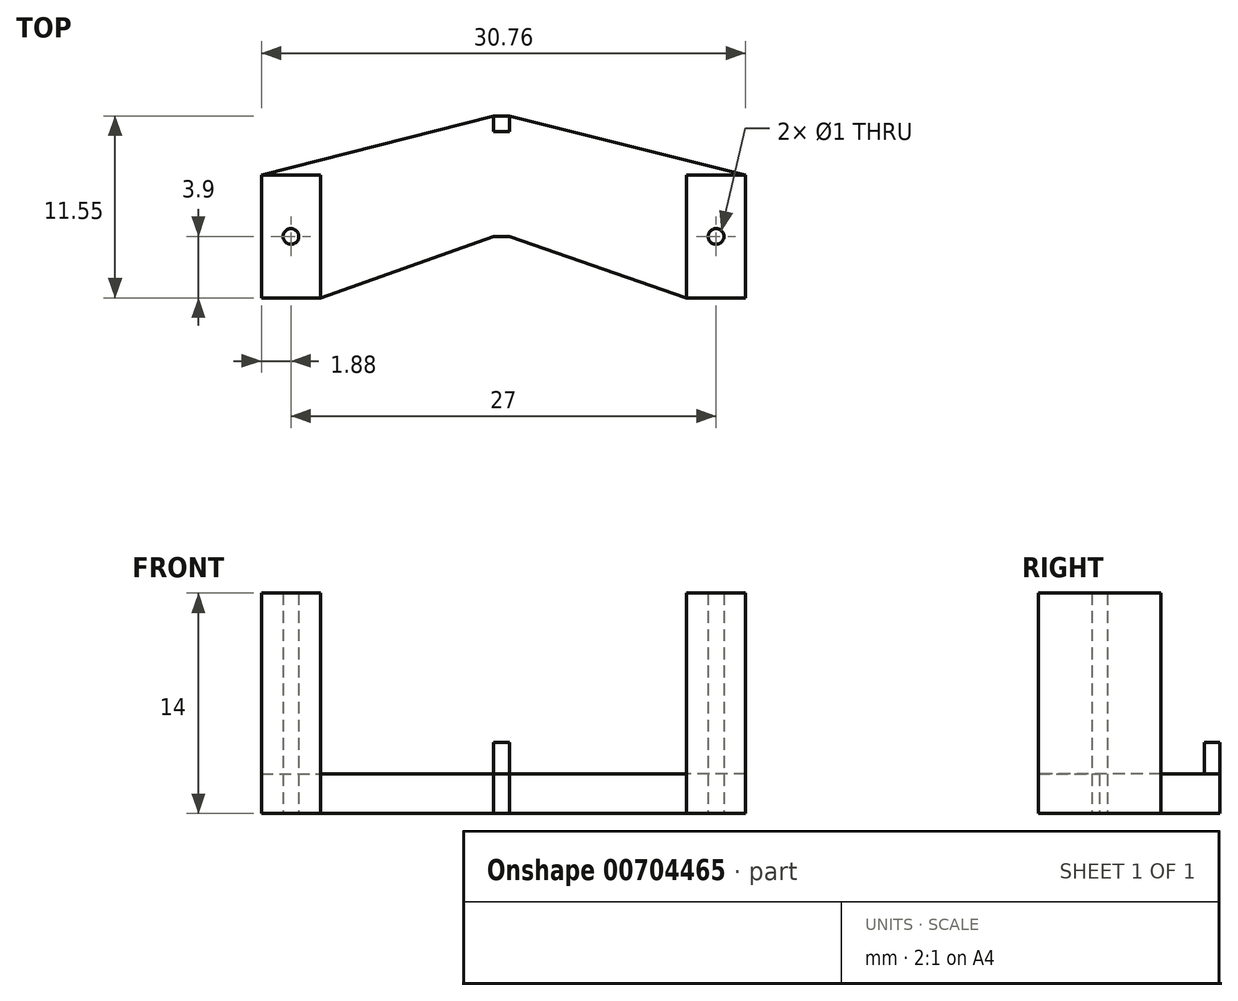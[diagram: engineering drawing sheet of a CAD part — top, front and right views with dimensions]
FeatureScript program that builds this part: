
annotation { "Feature Type Name" : "Feature", "Feature Type Description" : "" }
export const myFeature = defineFeature(function(context is Context, id is Id, definition is map)
    precondition{}
    {
        {
            var Q0;
            Q0=qCreatedBy(makeId("Top.planeOp"),FACE);
            var sketch = newSketch(context, id + "F0", { "sketchPlane" : qUnion([Q0])});
            skCircle(sketch, "E0", {"center": v(-13.5, 0) * mm, "radius": 0.5 * mm});
            skCircle(sketch, "E1", {"center": v(13.5, 0) * mm, "radius": 0.5 * mm});
            skLineSegment(sketch, "E2", {"start": v(-11.62, 3.9) * mm, "end": v(-11.63, -3.9) * mm});
            skLineSegment(sketch, "E3", {"start": v(11.62, 3.9) * mm, "end": v(11.63, -3.9) * mm});
            skLineSegment(sketch, "E4", {"start": v(11.62, 0) * mm, "end": v(15.37, 0) * mm, "construction": true});
            skLineSegment(sketch, "E5", {"start": v(15.38, 3.9) * mm, "end": v(15.38, -3.9) * mm});
            skLineSegment(sketch, "E6.MirrorCS", {"start": v(-15.38, 3.9) * mm, "end": v(-15.38, -3.9) * mm});
            skLineSegment(sketch, "E7", {"start": v(-15.38, 3.9) * mm, "end": v(-11.62, 3.9) * mm});
            skLineSegment(sketch, "E8", {"start": v(-11.63, -3.9) * mm, "end": v(-15.38, -3.9) * mm});
            skLineSegment(sketch, "E9", {"start": v(11.63, -3.9) * mm, "end": v(15.38, -3.9) * mm});
            skLineSegment(sketch, "E10", {"start": v(15.38, 3.9) * mm, "end": v(11.62, 3.9) * mm});
            skLineSegment(sketch, "E11", {"start": v(-0.62, 0) * mm, "end": v(-0.63, 7.65) * mm, "construction": true});
            skLineSegment(sketch, "E12.0", {"start": v(0.38, 0) * mm, "end": v(0.37, 7.65) * mm, "construction": true});
            skLineSegment(sketch, "E13", {"start": v(-11.62, 6.65) * mm, "end": v(11.62, 6.65) * mm, "construction": true});
            skLineSegment(sketch, "E14", {"start": v(-0.63, 7.65) * mm, "end": v(0.37, 7.65) * mm});
            skLineSegment(sketch, "E15", {"start": v(-0.63, 7.65) * mm, "end": v(-15.38, 3.9) * mm});
            skLineSegment(sketch, "E16", {"start": v(-11.62, -3.9) * mm, "end": v(-0.62, 0) * mm});
            skLineSegment(sketch, "E17", {"start": v(-0.62, 0) * mm, "end": v(0.38, 0) * mm});
            skLineSegment(sketch, "E18", {"start": v(0.38, 0) * mm, "end": v(11.62, -3.9) * mm});
            skLineSegment(sketch, "E19", {"start": v(0.37, 7.65) * mm, "end": v(15.38, 3.9) * mm});
            skLineSegment(sketch, "E20", {"start": v(-0.63, 7.65) * mm, "end": v(-0.63, 6.65) * mm});
            skLineSegment(sketch, "E21", {"start": v(-0.63, 6.65) * mm, "end": v(0.38, 6.65) * mm});
            skLineSegment(sketch, "E22", {"start": v(0.38, 6.65) * mm, "end": v(0.37, 7.65) * mm});
            skSolve(sketch);
        }
        {
            var Q0;
            Q0=makeQuery(id+"F0.imprint","IMPRINT",FACE,{"disambiguationData":[TD([[makeQuery(id+"F0.imprint","IMPRINT",EDGE,{"derivedFrom":sQuery(id+"F0.wireOp",EDGE,"E2")}),1.0]])]});
            var Q1;
            Q1=makeQuery(id+"F0.imprint","IMPRINT",FACE,{"disambiguationData":[TD([[makeQuery(id+"F0.imprint","IMPRINT",EDGE,{"derivedFrom":sQuery(id+"F0.wireOp",EDGE,"E14")}),-1.0]])]});
            var Q2;
            Q2=makeQuery(id+"F0.imprint","IMPRINT",FACE,{"disambiguationData":[TD([[makeQuery(id+"F0.imprint","IMPRINT",EDGE,{"derivedFrom":sQuery(id+"F0.wireOp",EDGE,"E0")}),-1.0]])]});
            var Q3;
            Q3=makeQuery(id+"F0.imprint","IMPRINT",FACE,{"disambiguationData":[TD([[makeQuery(id+"F0.imprint","IMPRINT",EDGE,{"derivedFrom":sQuery(id+"F0.wireOp",EDGE,"E1")}),-1.0]])]});
            extrude(context, id + "F1", {"entities" : qUnion([Q0, Q1, Q2, Q3]), "depth" : 2.5 * mm, "offsetDistance" : 25 * mm});
        }
        {
            var Q0;
            Q0=makeQuery(id+"F1.opExtrude","CAP_FACE",FACE,{"disambiguationData":[OSD([sQuery(id+"F0.wireOp",EDGE,"E0"),sQuery(id+"F0.wireOp",EDGE,"E1"),sQuery(id+"F0.wireOp",EDGE,"E5"),sQuery(id+"F0.wireOp",EDGE,"E6.MirrorCS"),sQuery(id+"F0.wireOp",EDGE,"E8"),sQuery(id+"F0.wireOp",EDGE,"E9"),sQuery(id+"F0.wireOp",EDGE,"E14"),sQuery(id+"F0.wireOp",EDGE,"E15"),sQuery(id+"F0.wireOp",EDGE,"E16"),sQuery(id+"F0.wireOp",EDGE,"E17"),sQuery(id+"F0.wireOp",EDGE,"E18"),sQuery(id+"F0.wireOp",EDGE,"E19")])],"isStart":false});
            var sketch = newSketch(context, id + "F2", { "sketchPlane" : qUnion([Q0])});
            skLineSegment(sketch, "E23.0", {"start": v(-15.38, 3.9) * mm, "end": v(-11.62, 3.9) * mm});
            skLineSegment(sketch, "E24.0", {"start": v(-11.62, 3.9) * mm, "end": v(-11.63, -3.9) * mm});
            skLineSegment(sketch, "E25.0", {"start": v(-11.63, -3.9) * mm, "end": v(-15.38, -3.9) * mm});
            skLineSegment(sketch, "E26.0", {"start": v(-15.38, 3.9) * mm, "end": v(-15.38, -3.9) * mm});
            skLineSegment(sketch, "E27.0", {"start": v(11.62, 3.9) * mm, "end": v(11.63, -3.9) * mm});
            skLineSegment(sketch, "E28.0", {"start": v(15.38, 3.9) * mm, "end": v(11.62, 3.9) * mm});
            skLineSegment(sketch, "E29.0", {"start": v(15.38, 3.9) * mm, "end": v(15.38, -3.9) * mm});
            skLineSegment(sketch, "E30.0", {"start": v(11.63, -3.9) * mm, "end": v(15.38, -3.9) * mm});
            skCircle(sketch, "E31.0", {"center": v(-13.5, 0) * mm, "radius": 0.5 * mm});
            skCircle(sketch, "E32.0", {"center": v(13.5, 0) * mm, "radius": 0.5 * mm});
            skSolve(sketch);
        }
        {
            var Q0;
            Q0=makeQuery(id+"F2.imprint","IMPRINT",FACE,{"disambiguationData":[TD([[makeQuery(id+"F2.imprint","IMPRINT",EDGE,{"derivedFrom":sQuery(id+"F2.wireOp",EDGE,"E23.0")}),-1.0]])]});
            var Q1;
            Q1=makeQuery(id+"F2.imprint","IMPRINT",FACE,{"disambiguationData":[TD([[makeQuery(id+"F2.imprint","IMPRINT",EDGE,{"derivedFrom":sQuery(id+"F2.wireOp",EDGE,"E27.0")}),1.0]])]});
            extrude(context, id + "F3", {"entities" : qUnion([Q0, Q1]), "operationType" : NewBodyOperationType.ADD, "depth" : 11.5 * mm, "offsetDistance" : 25 * mm});
        }
        {
            var Q0;
            Q0=makeQuery(id+"F1.opExtrude","CAP_FACE",FACE,{"disambiguationData":[OSD([sQuery(id+"F0.wireOp",EDGE,"E0"),sQuery(id+"F0.wireOp",EDGE,"E1"),sQuery(id+"F0.wireOp",EDGE,"E5"),sQuery(id+"F0.wireOp",EDGE,"E6.MirrorCS"),sQuery(id+"F0.wireOp",EDGE,"E8"),sQuery(id+"F0.wireOp",EDGE,"E9"),sQuery(id+"F0.wireOp",EDGE,"E14"),sQuery(id+"F0.wireOp",EDGE,"E15"),sQuery(id+"F0.wireOp",EDGE,"E16"),sQuery(id+"F0.wireOp",EDGE,"E17"),sQuery(id+"F0.wireOp",EDGE,"E18"),sQuery(id+"F0.wireOp",EDGE,"E19")])],"isStart":false});
            var sketch = newSketch(context, id + "F4", { "sketchPlane" : qUnion([Q0])});
            skLineSegment(sketch, "E33.0", {"start": v(-0.63, 7.65) * mm, "end": v(-0.63, 6.65) * mm});
            skLineSegment(sketch, "E34.0", {"start": v(-0.63, 7.65) * mm, "end": v(0.37, 7.65) * mm});
            skLineSegment(sketch, "E35.0", {"start": v(0.38, 6.65) * mm, "end": v(0.37, 7.65) * mm});
            skLineSegment(sketch, "E36.0", {"start": v(-0.63, 6.65) * mm, "end": v(0.38, 6.65) * mm});
            skSolve(sketch);
        }
        {
            var Q0;
            Q0 = qSketchRegion(id + "F4", true);
            extrude(context, id + "F5", {"entities" : qUnion([Q0]), "operationType" : NewBodyOperationType.ADD, "depth" : 2 * mm, "offsetDistance" : 25 * mm});
        }
    });
